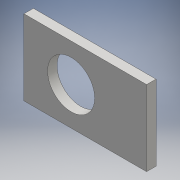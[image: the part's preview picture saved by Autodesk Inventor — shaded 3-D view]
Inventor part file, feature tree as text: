
AUTODESK INVENTOR PART (.ipt)
format: ipt  version: 2016 (Build 200138000, 138)  size: 103,424 bytes
history: native  units: mm
features: extrude x2, sketch x2
ambient origin geometry x8: Origin, YZ Plane, XZ Plane, XY Plane, X Axis, Y Axis, Z Axis, Center Point
bodies: Solid1 (feature_tree)
feature tree (4):
  extrude  "Extrusion1"  Depth=8.0mm
  extrude  "Extrusion2"  Depth=1.0mm
  sketch  "Sketch1"  dims[d0=13.0mm d1=8.0mm]
  sketch  "Sketch2"  dims[d2=1.0mm d3=0.0mm d4=5.0mm d5=5.0mm d6=1.0mm d7=0.0mm]
